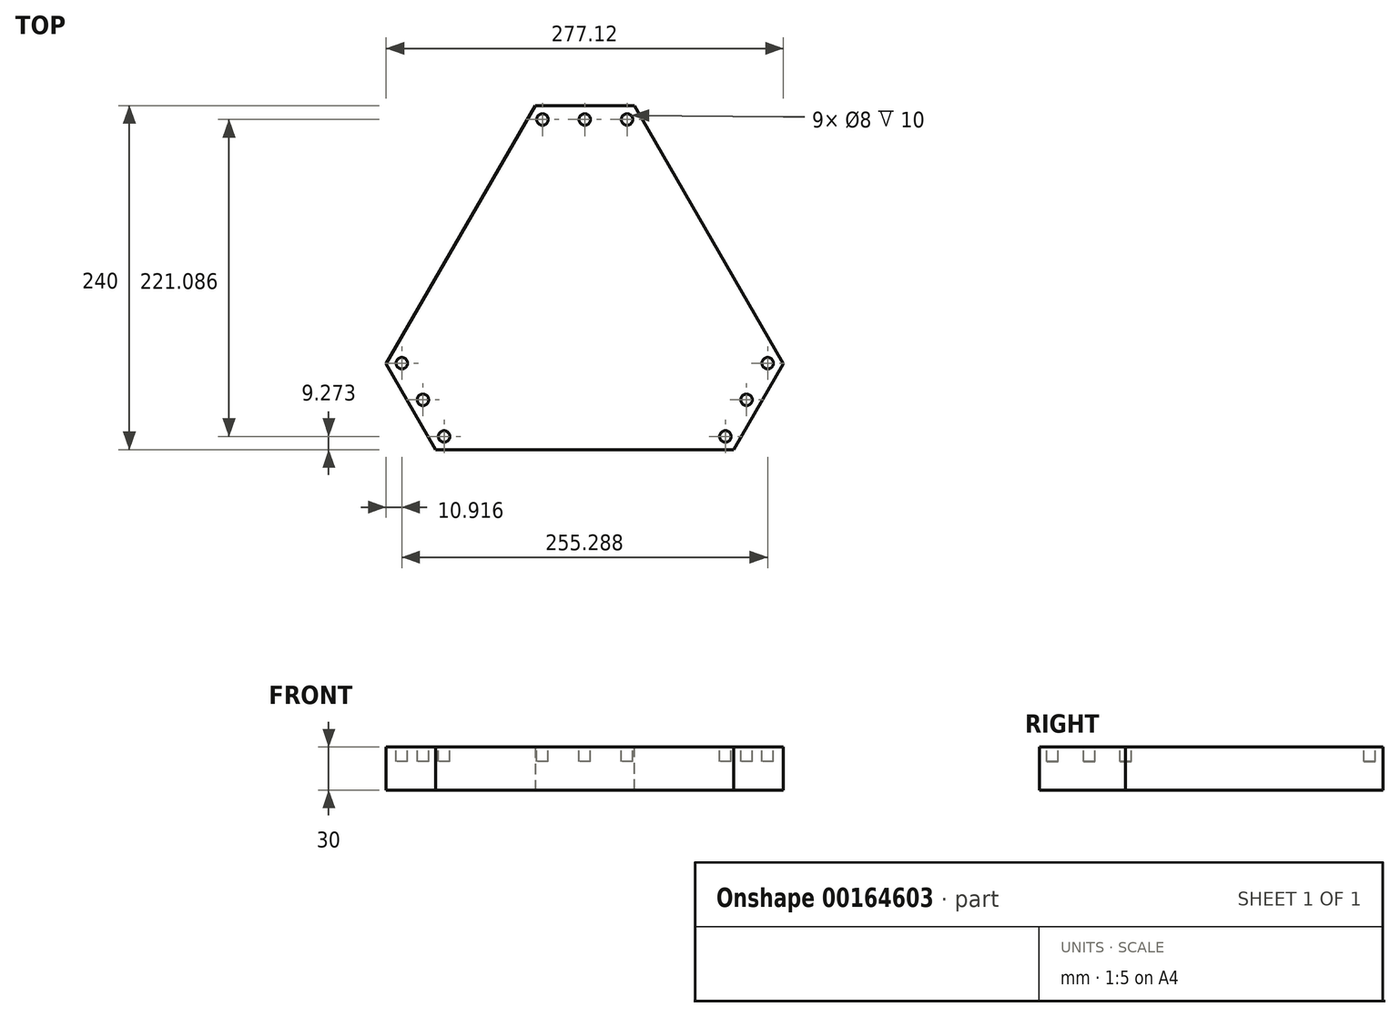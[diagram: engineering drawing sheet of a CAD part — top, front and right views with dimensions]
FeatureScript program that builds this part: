
annotation { "Feature Type Name" : "Feature", "Feature Type Description" : "" }
export const myFeature = defineFeature(function(context is Context, id is Id, definition is map)
    precondition{}
    {
        {
            var Q0;
            Q0=qCreatedBy(makeId("Top.planeOp"),FACE);
            var sketch = newSketch(context, id + "F0", { "sketchPlane" : qUnion([Q0])});
            skCircle(sketch, "E0.cCircle", {"center": v(0, 0) * mm, "radius": 100 * mm, "construction": true});
            skLineSegment(sketch, "E0.0", {"start": v(173.2, -100) * mm, "end": v(-173.2, -100) * mm});
            skLineSegment(sketch, "E0.1", {"start": v(-173.2, -100) * mm, "end": v(0, 200) * mm});
            skLineSegment(sketch, "E0.2", {"start": v(0, 200) * mm, "end": v(173.2, -100) * mm});
            skPoint(sketch, "E0.0.midPoint", {"position": v(0, -100) * mm});
            skSolve(sketch);
        }
        {
            var Q0;
            Q0 = qSketchRegion(id + "F0", true);
            extrude(context, id + "F1", {"entities" : qUnion([Q0]), "depth" : 30 * mm});
        }
        {
            var Q0;
            Q0=makeQuery(id+"F1.opExtrude","SWEPT_EDGE",EDGE,{"disambiguationData":[OSD([sQuery(id+"F0.wireOp",EDGE,"E0.0"),sQuery(id+"F0.wireOp",EDGE,"E0.1")])]});
            var Q1;
            Q1=makeQuery(id+"F1.opExtrude","SWEPT_EDGE",EDGE,{"disambiguationData":[OSD([sQuery(id+"F0.wireOp",EDGE,"E0.0"),sQuery(id+"F0.wireOp",EDGE,"E0.2")])]});
            var Q2;
            Q2=makeQuery(id+"F1.opExtrude","SWEPT_EDGE",EDGE,{"disambiguationData":[OSD([sQuery(id+"F0.wireOp",EDGE,"E0.1"),sQuery(id+"F0.wireOp",EDGE,"E0.2")])]});
            chamfer(context, id + "F2", {"entities" : qUnion([Q0, Q1, Q2]), "width" : 40 * mm, "tangentPropagation" : true});
        }
        {
            var Q0;
            Q0=makeQuery(id+"F1.opExtrude","CAP_FACE",FACE,{"disambiguationData":[OSD([sQuery(id+"F0.wireOp",EDGE,"E0.0"),sQuery(id+"F0.wireOp",EDGE,"E0.1"),sQuery(id+"F0.wireOp",EDGE,"E0.2")])],"isStart":false});
            var sketch = newSketch(context, id + "F3", { "sketchPlane" : qUnion([Q0])});
            skLineSegment(sketch, "E1.bottom", {"start": v(-21.5, 108.86) * mm, "end": v(21.5, 108.86) * mm, "construction": true});
            skLineSegment(sketch, "E1.top", {"start": v(-21.5, 151.86) * mm, "end": v(21.5, 151.86) * mm, "construction": true});
            skLineSegment(sketch, "E1.left", {"start": v(-21.5, 108.86) * mm, "end": v(-21.5, 151.86) * mm, "construction": true});
            skLineSegment(sketch, "E1.right", {"start": v(21.5, 108.86) * mm, "end": v(21.5, 151.86) * mm, "construction": true});
            skPoint(sketch, "E1.middle", {"position": v(0, 130.36) * mm});
            skCircle(sketch, "E2", {"center": v(-29.5, 130.36) * mm, "radius": 4 * mm});
            skPoint(sketch, "E2.centerSnap0", {"position": v(-21.5, 130.36) * mm});
            skCircle(sketch, "E3", {"center": v(29.5, 130.36) * mm, "radius": 4 * mm});
            skPoint(sketch, "E3.centerSnap0", {"position": v(21.5, 130.36) * mm});
            skCircle(sketch, "E4.1.0", {"center": v(-98.14, -90.73) * mm, "radius": 4 * mm});
            skCircle(sketch, "E4.1.1", {"center": v(-127.64, -39.63) * mm, "radius": 4 * mm});
            skCircle(sketch, "E4.2.0", {"center": v(127.64, -39.63) * mm, "radius": 4 * mm});
            skCircle(sketch, "E4.2.1", {"center": v(98.14, -90.73) * mm, "radius": 4 * mm});
            skPoint(sketch, "E4.center", {"position": v(0, 0) * mm});
            skCircle(sketch, "E5", {"center": v(0, 130.36) * mm, "radius": 4 * mm});
            skCircle(sketch, "E6.1.0", {"center": v(-112.9, -65.18) * mm, "radius": 4 * mm});
            skCircle(sketch, "E6.2.0", {"center": v(112.9, -65.18) * mm, "radius": 4 * mm});
            skSolve(sketch);
        }
        {
            var Q0;
            Q0 = qSketchRegion(id + "F3", true);
            extrude(context, id + "F4", {"entities" : qUnion([Q0]), "operationType" : NewBodyOperationType.REMOVE, "oppositeDirection" : true, "depth" : 10 * mm});
        }
    });
